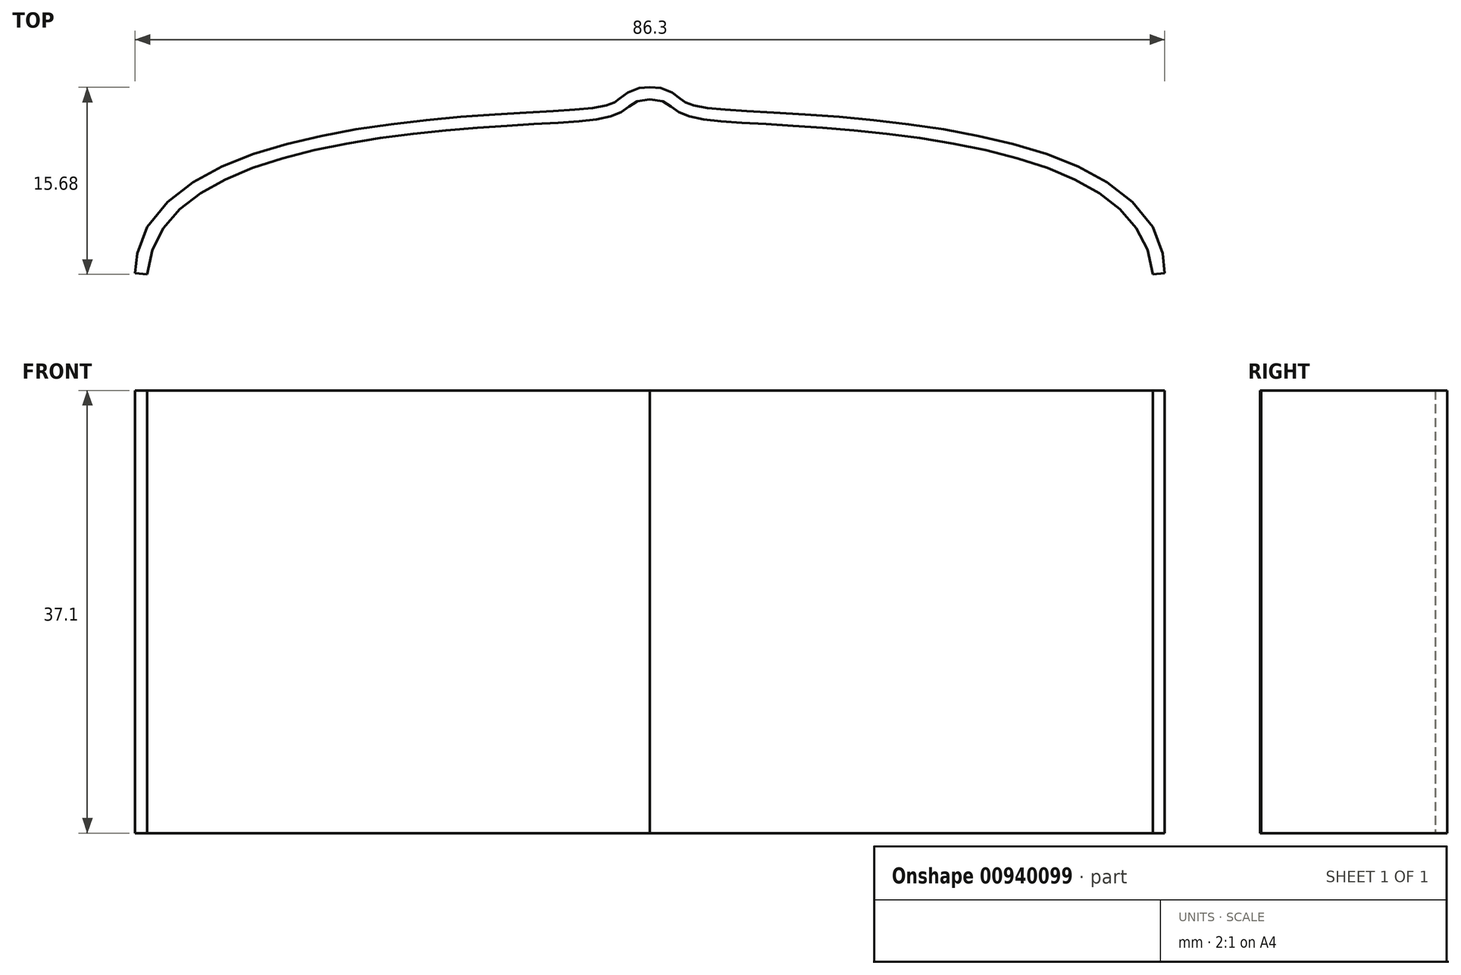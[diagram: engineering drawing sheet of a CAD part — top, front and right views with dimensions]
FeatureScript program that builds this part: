
annotation { "Feature Type Name" : "Feature", "Feature Type Description" : "" }
export const myFeature = defineFeature(function(context is Context, id is Id, definition is map)
    precondition{}
    {
        {
            var Q0;
            Q0=qCreatedBy(makeId("Top.planeOp"),FACE);
            var sketch = newSketch(context, id + "F0", { "sketchPlane" : qUnion([Q0])});
            skFitSpline(sketch, "E0", {"points": [v(-42.16, -0.55) * mm, v(-30.83, 9.17) * mm, v(-8.53, 12.12) * mm, v(-2.34, 13.08) * mm, v(0, 14.12) * mm], "startDerivative": vector(4.54, 50.98) * mm, "endDerivative": vector(31.24, -1.13) * mm});
            skFitSpline(sketch, "E1.MirrorCS", {"points": [v(42.16, -0.55) * mm, v(30.83, 9.17) * mm, v(8.53, 12.12) * mm, v(2.34, 13.08) * mm, v(0, 14.12) * mm], "startDerivative": vector(-4.54, 50.98) * mm, "endDerivative": vector(-31.24, -1.13) * mm});
            skFitSpline(sketch, "E2.0", {"points": [v(-43.15, -0.46) * mm, v(-43.05, 0.72) * mm, v(-42.42, 2.9) * mm, v(-40.42, 5.53) * mm, v(-37.66, 7.56) * mm, v(-34.34, 9.13) * mm, v(-30.63, 10.32) * mm, v(-26.66, 11.24) * mm, v(-22.58, 11.92) * mm, v(-18.53, 12.4) * mm, v(-14.65, 12.74) * mm, v(-11.1, 12.98) * mm, v(-8.53, 13.12) * mm, v(-6.78, 13.22) * mm, v(-5.64, 13.3) * mm, v(-4.66, 13.42) * mm, v(-3.99, 13.54) * mm, v(-3.54, 13.65) * mm, v(-3.26, 13.75) * mm, v(-3.07, 13.83) * mm, v(-2.93, 13.9) * mm, v(-2.85, 13.94) * mm, v(-2.77, 14) * mm, v(-2.65, 14.08) * mm, v(-2.49, 14.21) * mm, v(-2.24, 14.4) * mm, v(-1.94, 14.63) * mm, v(-1.55, 14.85) * mm, v(-1.09, 15.02) * mm, v(-0.56, 15.12) * mm, v(-0.17, 15.13) * mm, v(0.04, 15.12) * mm]});
            skFitSpline(sketch, "E3.0", {"points": [v(43.15, -0.46) * mm, v(43.05, 0.72) * mm, v(42.42, 2.9) * mm, v(40.42, 5.53) * mm, v(37.66, 7.56) * mm, v(34.34, 9.13) * mm, v(30.63, 10.32) * mm, v(26.66, 11.24) * mm, v(22.58, 11.92) * mm, v(18.53, 12.4) * mm, v(14.65, 12.74) * mm, v(11.1, 12.98) * mm, v(8.53, 13.12) * mm, v(6.78, 13.22) * mm, v(5.64, 13.3) * mm, v(4.66, 13.42) * mm, v(3.99, 13.54) * mm, v(3.54, 13.65) * mm, v(3.26, 13.75) * mm, v(3.07, 13.83) * mm, v(2.93, 13.9) * mm, v(2.85, 13.94) * mm, v(2.77, 14) * mm, v(2.65, 14.08) * mm, v(2.49, 14.21) * mm, v(2.24, 14.4) * mm, v(1.94, 14.63) * mm, v(1.55, 14.85) * mm, v(1.09, 15.02) * mm, v(0.56, 15.12) * mm, v(0.17, 15.13) * mm, v(-0.04, 15.12) * mm]});
            skLineSegment(sketch, "E4", {"start": v(-42.16, -0.55) * mm, "end": v(-43.15, -0.46) * mm});
            skLineSegment(sketch, "E5", {"start": v(42.16, -0.55) * mm, "end": v(43.15, -0.46) * mm});
            skSolve(sketch);
        }
        {
            var Q0;
            Q0 = qSketchRegion(id + "F0", true);
            extrude(context, id + "F1", {"entities" : qUnion([Q0]), "depth" : 37.1 * mm, "offsetDistance" : 25 * mm});
        }
    });
